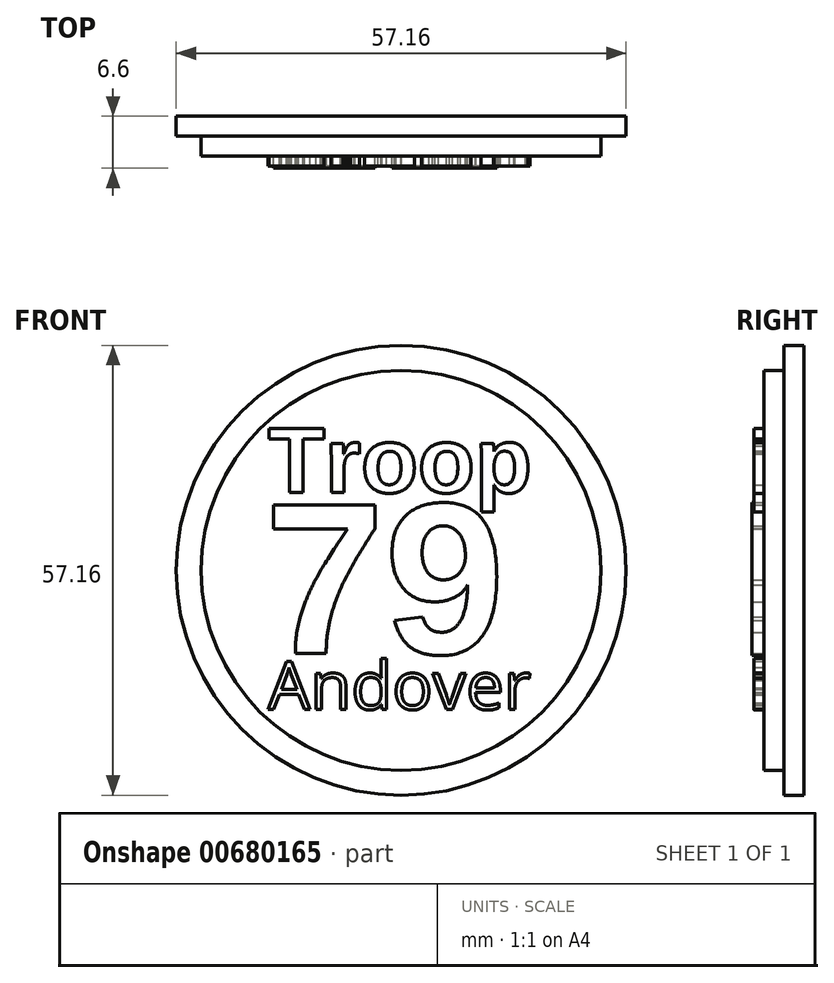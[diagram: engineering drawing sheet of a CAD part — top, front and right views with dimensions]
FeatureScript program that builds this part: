
annotation { "Feature Type Name" : "Feature", "Feature Type Description" : "" }
export const myFeature = defineFeature(function(context is Context, id is Id, definition is map)
    precondition{}
    {
        {
            var Q0;
            Q0=qCreatedBy(makeId("Front.planeOp"),FACE);
            var sketch = newSketch(context, id + "F0", { "sketchPlane" : qUnion([Q0])});
            skCircle(sketch, "E0", {"center": v(0, 0) * mm, "radius": 28.58 * mm});
            skSolve(sketch);
        }
        {
            var Q0;
            Q0=qCreatedBy(makeId("Front.planeOp"),FACE);
            var sketch = newSketch(context, id + "F1", { "sketchPlane" : qUnion([Q0])});
            skCircle(sketch, "E1", {"center": v(0, 0) * mm, "radius": 25.4 * mm});
            skSolve(sketch);
        }
        {
            var Q0;
            Q0 = qSketchRegion(id + "F1", true);
            extrude(context, id + "F2", {"entities" : qUnion([Q0]), "depth" : 2.54 * mm, "offsetDistance" : 25.4 * mm});
        }
        {
            var Q0;
            Q0=makeQuery(id+"F0.imprint","IMPRINT",FACE,{"disambiguationData":[TD([[makeQuery(id+"F0.imprint","IMPRINT",EDGE,{"derivedFrom":sQuery(id+"F0.wireOp",EDGE,"E0")}),1.0]])]});
            extrude(context, id + "F3", {"entities" : qUnion([Q0]), "operationType" : NewBodyOperationType.ADD, "oppositeDirection" : true, "depth" : 2.54 * mm, "offsetDistance" : 25.4 * mm});
        }
        {
            var Q0;
            Q0=makeQuery(id+"F2.opExtrude","CAP_FACE",FACE,{"disambiguationData":[OSD([sQuery(id+"F1.wireOp",EDGE,"E1")])],"isStart":false});
            var sketch = newSketch(context, id + "F4", { "sketchPlane" : qUnion([Q0])});
            skText(sketch, "E2", { "text": "79", "fontName": "Arimo-Bold.ttf"});
            const initialGuessF4  = {"E2": [-0.01738, -0.01057, 1, 0, 0.01977]};
            skSetInitialGuess(sketch, initialGuessF4);
            skSolve(sketch);
        }
        {
            var Q0;
            Q0=qCreatedBy(makeId("Front.planeOp"),FACE);
            var sketch = newSketch(context, id + "F5", { "sketchPlane" : qUnion([Q0])});
            skText(sketch, "E3", { "text": "Troop", "fontName": "Arimo-Bold.ttf"});
            const initialGuessF5  = {"E3": [-0.01693, 0.00987, 1, 0, 0.00852]};
            skSetInitialGuess(sketch, initialGuessF5);
            skSolve(sketch);
        }
        {
            var Q0;
            Q0=qCreatedBy(makeId("Front.planeOp"),FACE);
            var sketch = newSketch(context, id + "F6", { "sketchPlane" : qUnion([Q0])});
            skText(sketch, "E4", { "text": "Andover", "fontName": "OpenSans-Regular.ttf"});
            const initialGuessF6  = {"E4": [-0.01693, -0.01768, 1, 0, 0.00612]};
            skSetInitialGuess(sketch, initialGuessF6);
            skSolve(sketch);
        }
        {
            var Q0;
            Q0 = qSketchRegion(id + "F5", true);
            extrude(context, id + "F7", {"entities" : qUnion([Q0]), "operationType" : NewBodyOperationType.ADD, "depth" : 3.8 * mm, "offsetDistance" : 25.4 * mm});
        }
        {
            var Q0;
            Q0 = qSketchRegion(id + "F4", true);
            extrude(context, id + "F8", {"entities" : qUnion([Q0]), "operationType" : NewBodyOperationType.ADD, "depth" : 1.52 * mm, "offsetDistance" : 25.4 * mm});
        }
        {
            var Q0;
            Q0 = qSketchRegion(id + "F6", true);
            extrude(context, id + "F9", {"entities" : qUnion([Q0]), "operationType" : NewBodyOperationType.ADD, "depth" : 3.8 * mm, "offsetDistance" : 25.4 * mm});
        }
    });
